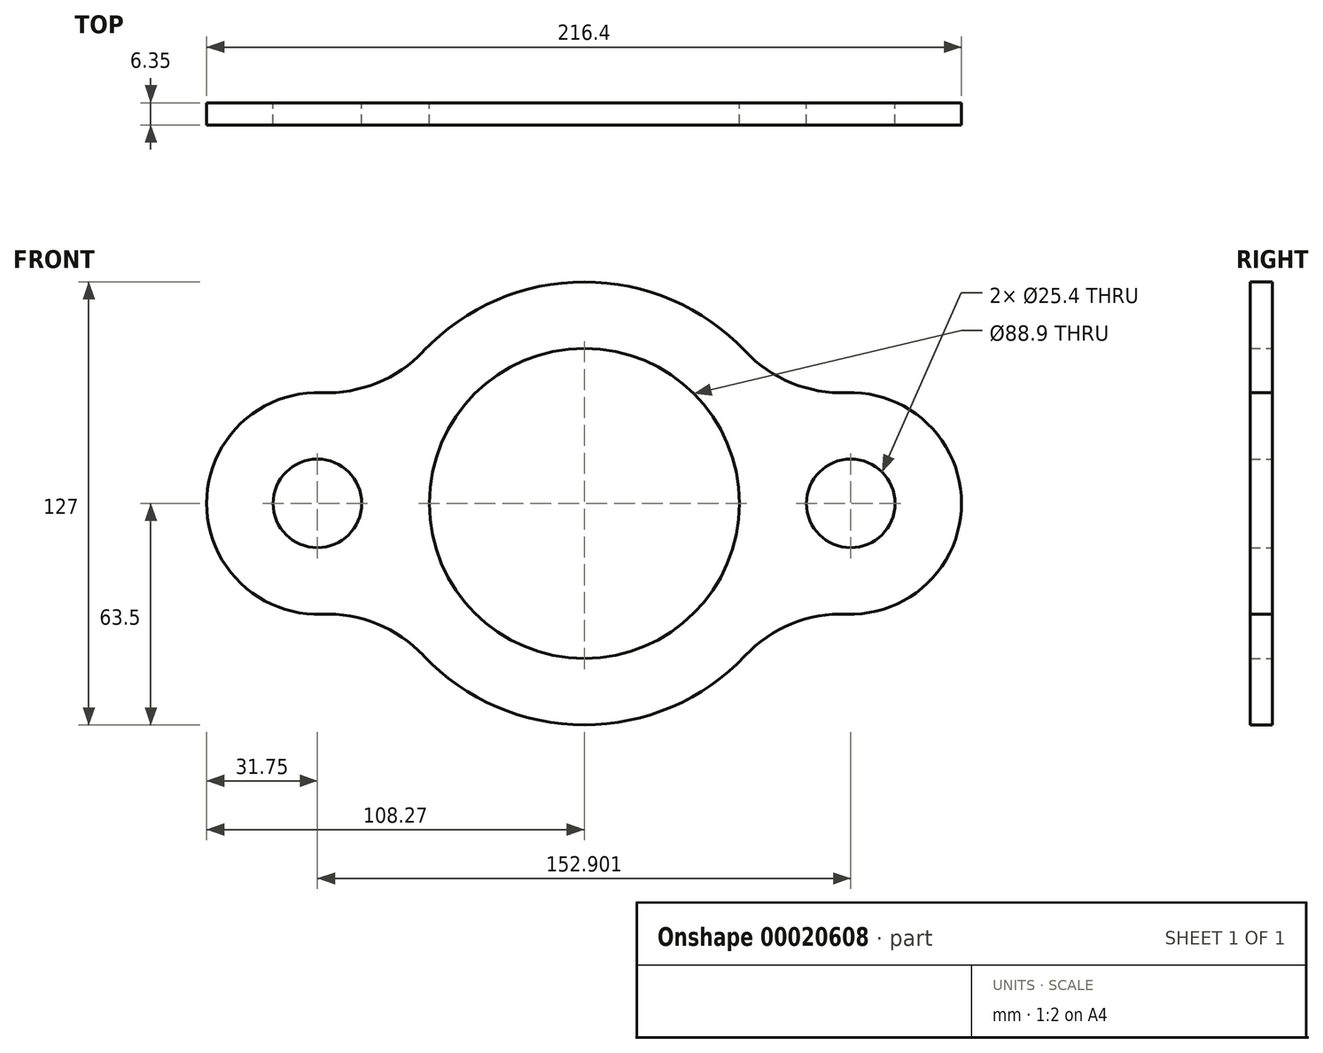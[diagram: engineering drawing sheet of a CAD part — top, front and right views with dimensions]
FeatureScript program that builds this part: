
annotation { "Feature Type Name" : "Feature", "Feature Type Description" : "" }
export const myFeature = defineFeature(function(context is Context, id is Id, definition is map)
    precondition{}
    {
        {
            var Q0;
            Q0=qCreatedBy(makeId("Front.planeOp"),FACE);
            var sketch = newSketch(context, id + "F0", { "sketchPlane" : qUnion([Q0])});
            skCircle(sketch, "E0", {"center": v(0, 0) * mm, "radius": 44.45 * mm});
            skArc(sketch, "E1", {"start": v(-46.14, -43.62) * mm, "mid": v(0, -63.5) * mm, "end": v(46.14, -43.63) * mm});
            skLineSegment(sketch, "E2", {"start": v(44.45, 0) * mm, "end": v(44.63, 0) * mm, "construction": true});
            skArc(sketch, "E3", {"start": v(-75.3, 31.73) * mm, "mid": v(-108.27, 0) * mm, "end": v(-75.3, -31.73) * mm});
            skArc(sketch, "E4", {"start": v(75.22, -31.73) * mm, "mid": v(108.13, 0) * mm, "end": v(75.22, 31.73) * mm});
            skArc(sketch, "E5.trimOffspring", {"start": v(46.14, 43.63) * mm, "mid": v(0, 63.5) * mm, "end": v(-46.14, 43.62) * mm});
            skPoint(sketch, "E6.visualSharp", {"position": v(-58.02, 25.8) * mm});
            skArc(sketch, "E6.filletArc", {"start": v(-75.3, 31.73) * mm, "mid": v(-59.43, 34.52) * mm, "end": v(-46.14, 43.62) * mm});
            skPoint(sketch, "E7.visualSharp", {"position": v(57.99, 25.88) * mm});
            skArc(sketch, "E7.filletArc", {"start": v(46.14, 43.63) * mm, "mid": v(59.4, 34.54) * mm, "end": v(75.22, 31.73) * mm});
            skPoint(sketch, "E8.visualSharp", {"position": v(-58.02, -25.8) * mm});
            skArc(sketch, "E8.filletArc", {"start": v(-46.14, -43.62) * mm, "mid": v(-59.43, -34.52) * mm, "end": v(-75.3, -31.73) * mm});
            skPoint(sketch, "E9.visualSharp", {"position": v(57.99, -25.88) * mm});
            skArc(sketch, "E9.filletArc", {"start": v(75.22, -31.73) * mm, "mid": v(59.4, -34.54) * mm, "end": v(46.14, -43.63) * mm});
            skCircle(sketch, "E10", {"center": v(-76.52, 0) * mm, "radius": 12.7 * mm});
            skCircle(sketch, "E11", {"center": v(76.38, 0) * mm, "radius": 12.7 * mm});
            skSolve(sketch);
        }
        {
            var Q0;
            Q0=makeQuery(id+"F0.imprint","IMPRINT",FACE,{"disambiguationData":[TD([[makeQuery(id+"F0.imprint","IMPRINT",EDGE,{"derivedFrom":sQuery(id+"F0.wireOp",EDGE,"E0")}),-1.0]])]});
            extrude(context, id + "F1", {"entities" : qUnion([Q0]), "depth" : 6.35 * mm});
        }
    });
